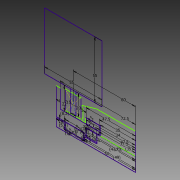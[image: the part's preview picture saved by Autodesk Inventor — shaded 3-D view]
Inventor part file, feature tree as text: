
AUTODESK INVENTOR PART (.ipt)
format: ipt  version: 2020 (Build 240168000, 168)  size: 131,584 bytes
history: native  units: mm
features: sketch x1
ambient origin geometry x8: Origin, YZ Plane, XZ Plane, XY Plane, X Axis, Y Axis, Z Axis, Center Point
feature tree (1):
  sketch  "Sketch1"  dims[d4=47.5mm d5=35.0mm d6=5.0mm d7=7.0mm d8=37.5mm d9=47.5mm d12=50.0mm d13=67.5mm d14=6.0mm d17=4.0mm d19=55.0mm d20=55.0mm d21=20.0mm d22=5.0mm d23=72.5mm d24=60.0mm d25=22.0mm d26=15.0mm d27=1.0mm d29=0.2mm d30=2.0mm d31=0.2mm d32=1.0mm d33=1.0mm d35=0.2mm d36=0.2mm d37=0.2mm d38=1.0mm d39=1.0mm d40=0.5mm d41=0.5mm d42=3.0mm d43=0.2mm d44=0.2mm d45=3.0mm d46=1.0mm d47=0.2mm d48=35.0mm d49=47.7mm d50=7.2mm d51=8.2mm d52=1.3mm d53=8.0mm d54=5.4mm d55=19.5mm d56=49.0mm d57=34.0mm]
